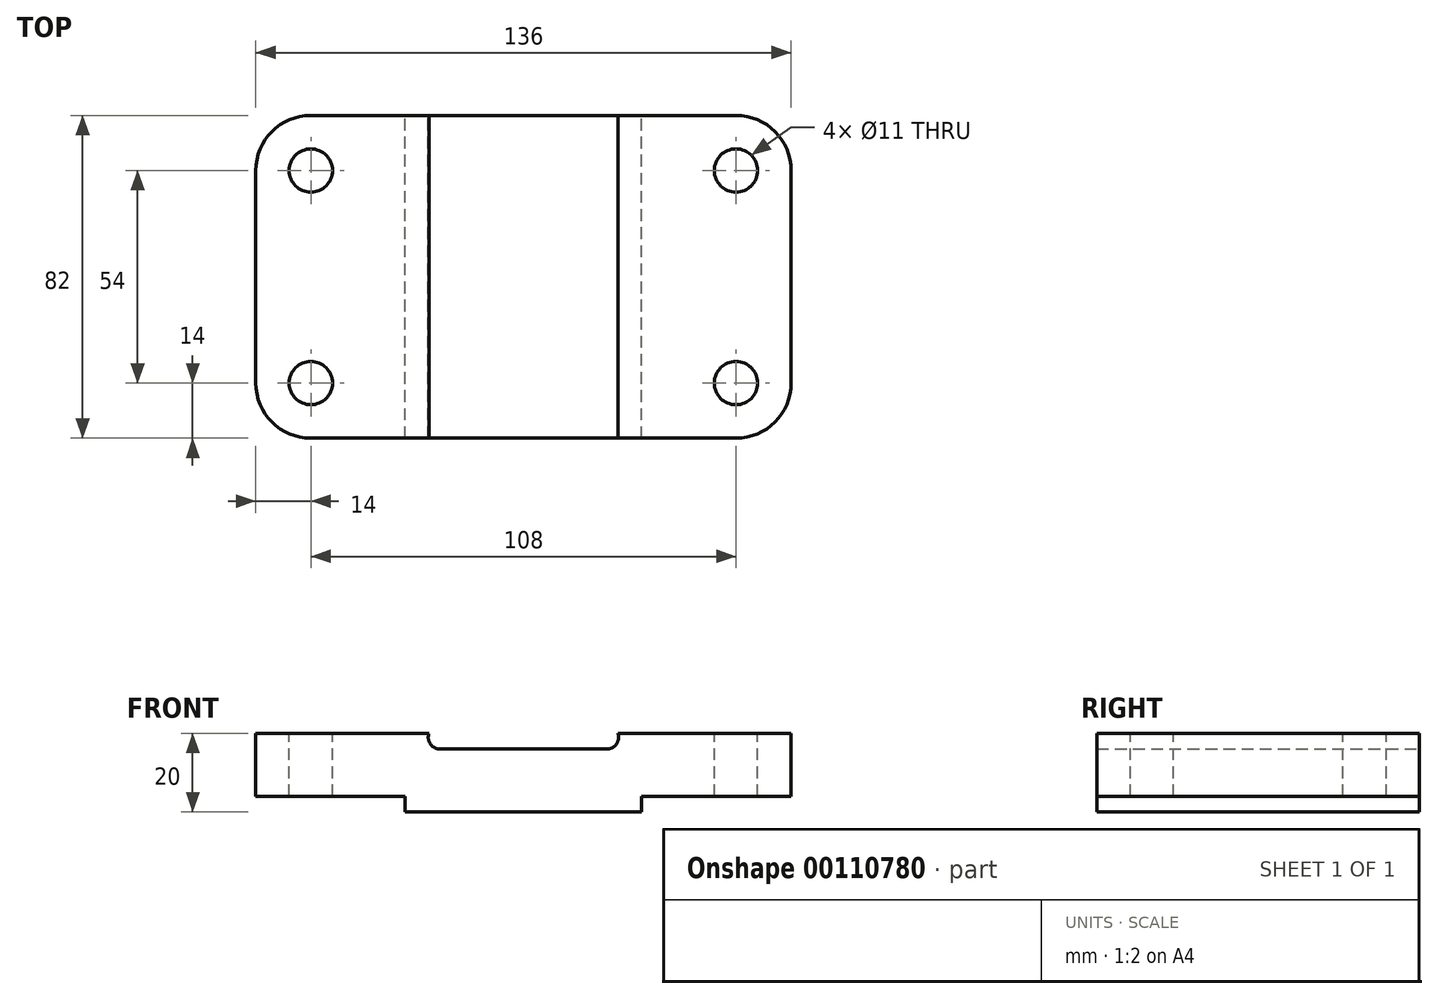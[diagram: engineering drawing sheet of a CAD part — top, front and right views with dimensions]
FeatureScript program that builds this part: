
annotation { "Feature Type Name" : "Feature", "Feature Type Description" : "" }
export const myFeature = defineFeature(function(context is Context, id is Id, definition is map)
    precondition{}
    {
        {
            var Q0;
            Q0=qCreatedBy(makeId("Front.planeOp"),FACE);
            var sketch = newSketch(context, id + "F0", { "sketchPlane" : qUnion([Q0])});
            skLineSegment(sketch, "E0", {"start": v(0, 0) * mm, "end": v(38, 0) * mm});
            skLineSegment(sketch, "E1", {"start": v(38, 0) * mm, "end": v(38, -4) * mm});
            skLineSegment(sketch, "E2", {"start": v(38, -4) * mm, "end": v(98, -4) * mm});
            skLineSegment(sketch, "E3", {"start": v(98, -4) * mm, "end": v(98, 0) * mm});
            skLineSegment(sketch, "E4", {"start": v(98, 0) * mm, "end": v(136, 0) * mm});
            skLineSegment(sketch, "E5", {"start": v(136, 0) * mm, "end": v(136, 16) * mm});
            skLineSegment(sketch, "E6", {"start": v(136, 16) * mm, "end": v(92, 16) * mm});
            skLineSegment(sketch, "E7", {"start": v(44, 16) * mm, "end": v(0, 16) * mm});
            skLineSegment(sketch, "E8", {"start": v(0, 16) * mm, "end": v(0, 0) * mm});
            skLineSegment(sketch, "E9", {"start": v(46.83, 12) * mm, "end": v(89.17, 12) * mm});
            skArc(sketch, "E10", {"start": v(89.17, 12) * mm, "mid": v(91.62, 13.27) * mm, "end": v(92, 16) * mm});
            skArc(sketch, "E11", {"start": v(44, 16) * mm, "mid": v(44.38, 13.27) * mm, "end": v(46.83, 12) * mm});
            skSolve(sketch);
        }
        {
            var Q0;
            Q0 = qSketchRegion(id + "F0", true);
            extrude(context, id + "F1", {"entities" : qUnion([Q0]), "depth" : 82 * mm});
        }
        {
            var Q0;
            Q0=makeQuery(id+"F1.opExtrude","SWEPT_FACE",FACE,{"disambiguationData":[OSD([sQuery(id+"F0.wireOp",EDGE,"E7")])]});
            var sketch = newSketch(context, id + "F2", { "sketchPlane" : qUnion([Q0])});
            skCircle(sketch, "E12", {"center": v(14, -14) * mm, "radius": 5.5 * mm});
            skCircle(sketch, "E13", {"center": v(14, -68) * mm, "radius": 5.5 * mm});
            skCircle(sketch, "E14", {"center": v(122, -14) * mm, "radius": 5.5 * mm});
            skCircle(sketch, "E15", {"center": v(122, -68) * mm, "radius": 5.5 * mm});
            skSolve(sketch);
        }
        {
            var Q0;
            Q0 = qSketchRegion(id + "F2", true);
            extrude(context, id + "F3", {"entities" : qUnion([Q0]), "operationType" : NewBodyOperationType.REMOVE, "endBound" : BoundingType.THROUGH_ALL, "oppositeDirection" : true, "depth" : 25 * mm});
        }
        {
            var Q0;
            Q0=makeQuery(id+"F1.opExtrude","SWEPT_FACE",FACE,{"disambiguationData":[OSD([sQuery(id+"F0.wireOp",EDGE,"E7")])]});
            var sketch = newSketch(context, id + "F4", { "sketchPlane" : qUnion([Q0])});
            skLineSegment(sketch, "E16", {"start": v(0, 0) * mm, "end": v(0, -14) * mm});
            skLineSegment(sketch, "E17", {"start": v(0, 0) * mm, "end": v(14, 0) * mm});
            skLineSegment(sketch, "E18", {"start": v(0, -82) * mm, "end": v(0, -68) * mm});
            skLineSegment(sketch, "E19", {"start": v(0, -82) * mm, "end": v(14, -82) * mm});
            skLineSegment(sketch, "E20", {"start": v(122, 0) * mm, "end": v(136, 0) * mm});
            skLineSegment(sketch, "E21", {"start": v(136, 0) * mm, "end": v(136, -14) * mm});
            skLineSegment(sketch, "E22", {"start": v(136, -68) * mm, "end": v(136, -82) * mm});
            skLineSegment(sketch, "E23", {"start": v(136, -82) * mm, "end": v(122, -82) * mm});
            skArc(sketch, "E24", {"start": v(14, 0) * mm, "mid": v(4.1, -4.1) * mm, "end": v(0, -14) * mm});
            skArc(sketch, "E25", {"start": v(0, -68) * mm, "mid": v(4.1, -77.9) * mm, "end": v(14, -82) * mm});
            skArc(sketch, "E26", {"start": v(122, 0) * mm, "mid": v(131.9, -4.1) * mm, "end": v(136, -14) * mm});
            skArc(sketch, "E27", {"start": v(122, -82) * mm, "mid": v(131.9, -77.9) * mm, "end": v(136, -68) * mm});
            skSolve(sketch);
        }
        {
            var Q0;
            Q0 = qSketchRegion(id + "F4", true);
            extrude(context, id + "F5", {"entities" : qUnion([Q0]), "operationType" : NewBodyOperationType.REMOVE, "endBound" : BoundingType.THROUGH_ALL, "oppositeDirection" : true, "depth" : 25 * mm});
        }
    });
